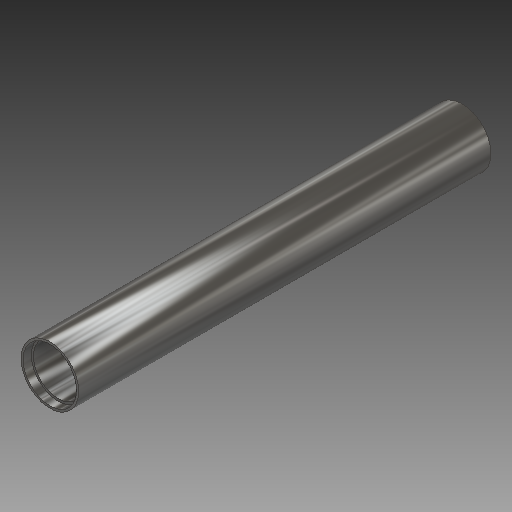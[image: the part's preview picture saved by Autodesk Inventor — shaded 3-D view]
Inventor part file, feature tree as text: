
AUTODESK INVENTOR PART (.ipt)
format: ipt  version: 2019 (Build 230136000, 136)  size: 153,088 bytes
history: native  units: mm
features: extrude x3, sketch x3, plane x1, mirror x1
ambient origin geometry x8: Origin, YZ Plane, XZ Plane, XY Plane, X Axis, Y Axis, Z Axis, Center Point
bodies: Solid1 (feature_tree)
feature tree (8):
  extrude  "Extrusion1"  Depth=500.0mm TaperAngle=0.0deg
  extrude  "Extrusion2"  Depth=500.0mm TaperAngle=0.0deg
  extrude  "Extrusion3"  Depth=10.0mm TaperAngle=0.0deg
  plane  "Work Plane2"
  mirror  "Mirror2"
  sketch  "Sketch1"  dims[d0=70.0mm d1=500.0mm d2=0.0mm]
  sketch  "Sketch2"  dims[d3=60.0mm d4=500.0mm d5=0.0mm]
  sketch  "Sketch3"  dims[d6=65.0mm d7=10.0mm d8=0.0mm]
